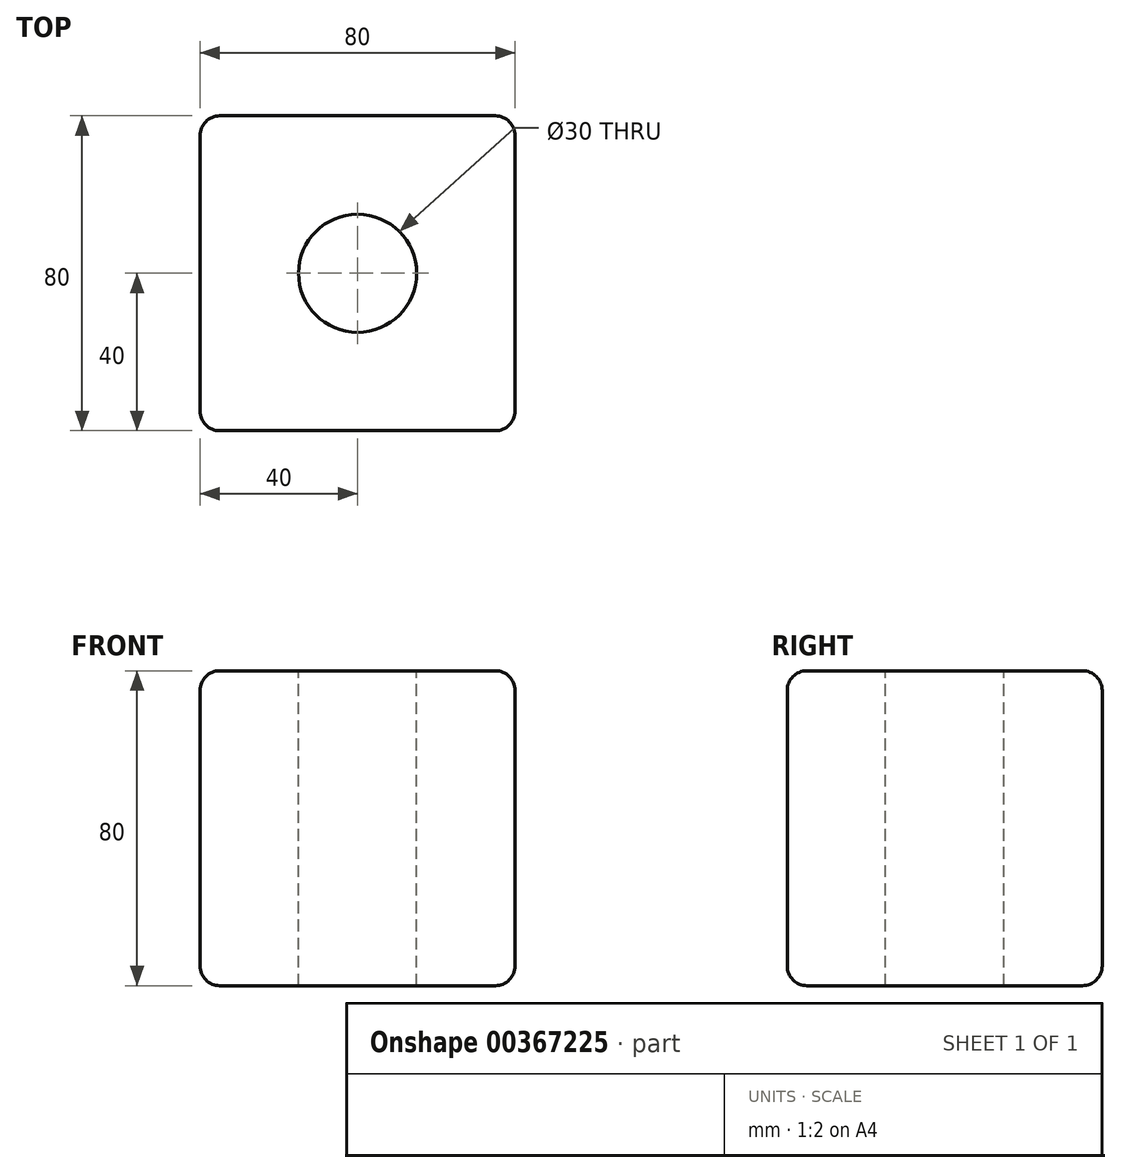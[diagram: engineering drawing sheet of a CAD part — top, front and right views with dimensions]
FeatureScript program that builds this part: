
annotation { "Feature Type Name" : "Feature", "Feature Type Description" : "" }
export const myFeature = defineFeature(function(context is Context, id is Id, definition is map)
    precondition{}
    {
        {
            var Q0;
            Q0=qCreatedBy(makeId("Top.planeOp"),FACE);
            var sketch = newSketch(context, id + "F0", { "sketchPlane" : qUnion([Q0])});
            skLineSegment(sketch, "E0.bottom", {"start": v(-40, 40) * mm, "end": v(40, 40) * mm});
            skLineSegment(sketch, "E0.top", {"start": v(-40, -40) * mm, "end": v(40, -40) * mm});
            skLineSegment(sketch, "E0.left", {"start": v(-40, 40) * mm, "end": v(-40, -40) * mm});
            skLineSegment(sketch, "E0.right", {"start": v(40, 40) * mm, "end": v(40, -40) * mm});
            skPoint(sketch, "E0.middle", {"position": v(0, 0) * mm});
            skSolve(sketch);
        }
        {
            var Q0;
            Q0=makeQuery(id+"F0.imprint","IMPRINT",FACE,{"disambiguationData":[TD([[makeQuery(id+"F0.imprint","IMPRINT",EDGE,{"derivedFrom":sQuery(id+"F0.wireOp",EDGE,"E0.bottom")}),-1.0]])]});
            extrude(context, id + "F1", {"entities" : qUnion([Q0]), "depth" : 80 * mm});
        }
        {
            var Q0;
            Q0=makeQuery(id+"F1.opExtrude","CAP_FACE",FACE,{"disambiguationData":[OSD([sQuery(id+"F0.wireOp",EDGE,"E0.bottom"),sQuery(id+"F0.wireOp",EDGE,"E0.top"),sQuery(id+"F0.wireOp",EDGE,"E0.left"),sQuery(id+"F0.wireOp",EDGE,"E0.right")])],"isStart":false});
            var sketch = newSketch(context, id + "F2", { "sketchPlane" : qUnion([Q0])});
            skCircle(sketch, "E1", {"center": v(0, 0) * mm, "radius": 15 * mm});
            skSolve(sketch);
        }
        {
            var Q0;
            Q0=makeQuery(id+"F2.imprint","IMPRINT",FACE,{"disambiguationData":[TD([[makeQuery(id+"F2.imprint","IMPRINT",EDGE,{"derivedFrom":sQuery(id+"F2.wireOp",EDGE,"E1")}),1.0]])]});
            extrude(context, id + "F3", {"entities" : qUnion([Q0]), "operationType" : NewBodyOperationType.REMOVE, "endBound" : BoundingType.THROUGH_ALL, "oppositeDirection" : true, "depth" : 25 * mm});
        }
        {
            var Q0;
            Q0=makeQuery(id+"F1.opExtrude","CAP_EDGE",EDGE,{"disambiguationData":[OSD([sQuery(id+"F0.wireOp",EDGE,"E0.bottom")])],"isStart":false});
            var Q1;
            Q1=makeQuery(id+"F1.opExtrude","CAP_EDGE",EDGE,{"disambiguationData":[OSD([sQuery(id+"F0.wireOp",EDGE,"E0.left")])],"isStart":false});
            var Q2;
            Q2=makeQuery(id+"F1.opExtrude","CAP_EDGE",EDGE,{"disambiguationData":[OSD([sQuery(id+"F0.wireOp",EDGE,"E0.right")])],"isStart":false});
            var Q3;
            Q3=makeQuery(id+"F1.opExtrude","CAP_EDGE",EDGE,{"disambiguationData":[OSD([sQuery(id+"F0.wireOp",EDGE,"E0.top")])],"isStart":false});
            var Q4;
            Q4=makeQuery(id+"F1.opExtrude","SWEPT_EDGE",EDGE,{"disambiguationData":[OSD([sQuery(id+"F0.wireOp",EDGE,"E0.top"),sQuery(id+"F0.wireOp",EDGE,"E0.left")])]});
            var Q5;
            Q5=makeQuery(id+"F1.opExtrude","CAP_EDGE",EDGE,{"disambiguationData":[OSD([sQuery(id+"F0.wireOp",EDGE,"E0.left")])],"isStart":true});
            var Q6;
            Q6=makeQuery(id+"F1.opExtrude","SWEPT_EDGE",EDGE,{"disambiguationData":[OSD([sQuery(id+"F0.wireOp",EDGE,"E0.bottom"),sQuery(id+"F0.wireOp",EDGE,"E0.left")])]});
            var Q7;
            Q7=makeQuery(id+"F1.opExtrude","SWEPT_EDGE",EDGE,{"disambiguationData":[OSD([sQuery(id+"F0.wireOp",EDGE,"E0.bottom"),sQuery(id+"F0.wireOp",EDGE,"E0.right")])]});
            var Q8;
            Q8=makeQuery(id+"F1.opExtrude","CAP_EDGE",EDGE,{"disambiguationData":[OSD([sQuery(id+"F0.wireOp",EDGE,"E0.right")])],"isStart":true});
            var Q9;
            Q9=makeQuery(id+"F1.opExtrude","SWEPT_EDGE",EDGE,{"disambiguationData":[OSD([sQuery(id+"F0.wireOp",EDGE,"E0.top"),sQuery(id+"F0.wireOp",EDGE,"E0.right")])]});
            var Q10;
            Q10=makeQuery(id+"F1.opExtrude","CAP_EDGE",EDGE,{"disambiguationData":[OSD([sQuery(id+"F0.wireOp",EDGE,"E0.bottom")])],"isStart":true});
            var Q11;
            Q11=makeQuery(id+"F1.opExtrude","CAP_EDGE",EDGE,{"disambiguationData":[OSD([sQuery(id+"F0.wireOp",EDGE,"E0.top")])],"isStart":true});
            fillet(context, id + "F4", {"entities" : qUnion([Q0, Q1, Q2, Q3, Q4, Q5, Q6, Q7, Q8, Q9, Q10, Q11]), "radius" : 5 * mm, "tangentPropagation" : true, "allowEdgeOverflow" : false});
        }
    });
